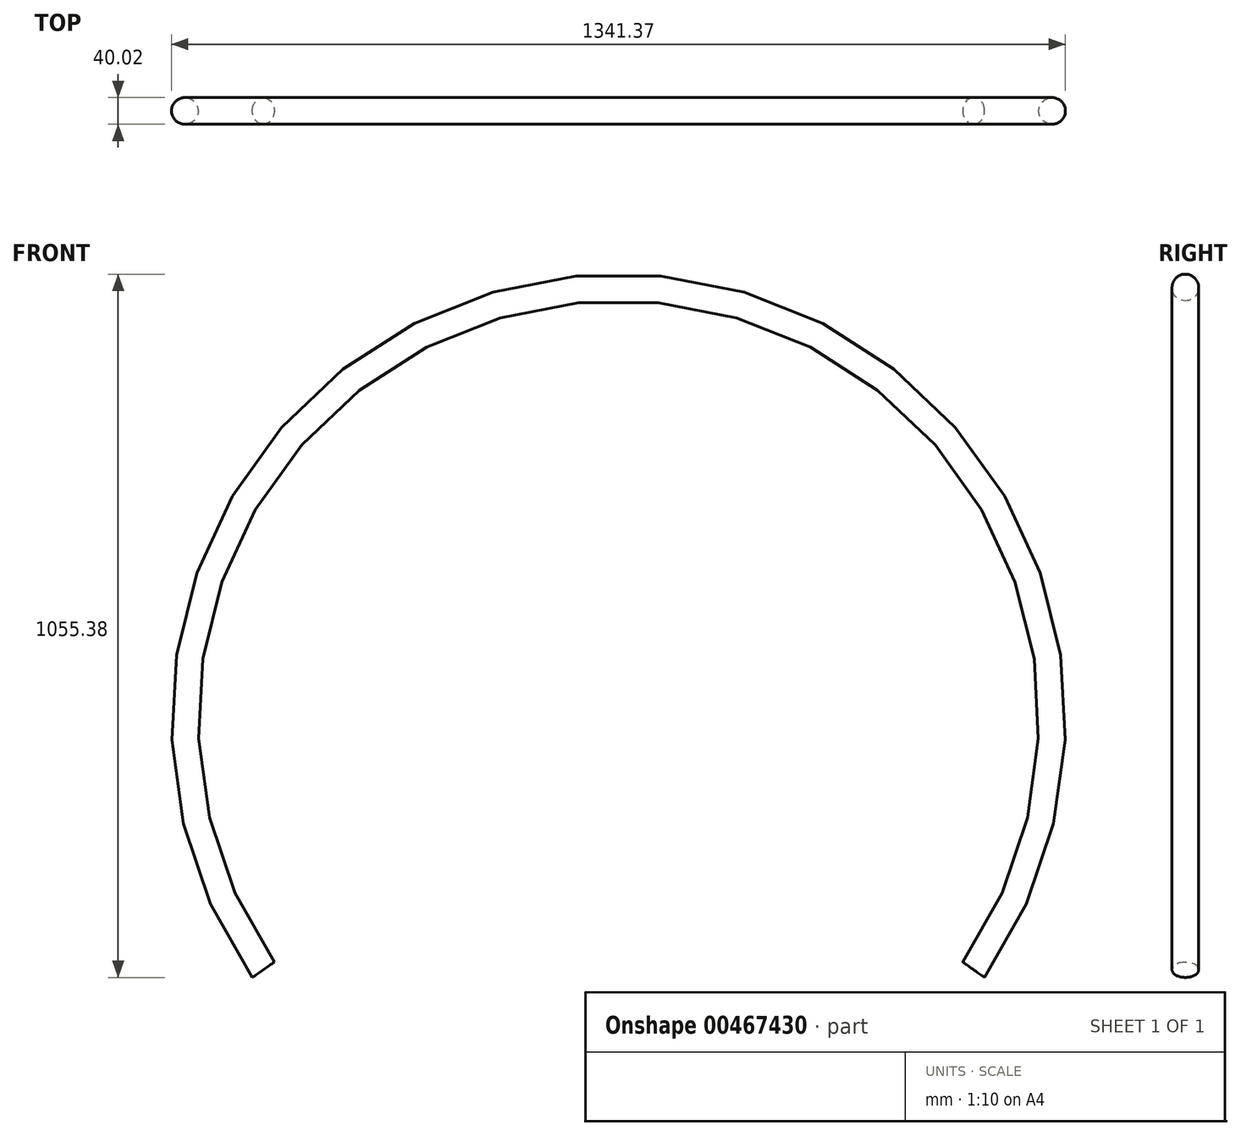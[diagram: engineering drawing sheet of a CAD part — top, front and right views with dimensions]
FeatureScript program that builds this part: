
annotation { "Feature Type Name" : "Feature", "Feature Type Description" : "" }
export const myFeature = defineFeature(function(context is Context, id is Id, definition is map)
    precondition{}
    {
        {
            var Q0;
            Q0=qCreatedBy(makeId("Top.planeOp"),FACE);
            var sketch = newSketch(context, id + "F0", { "sketchPlane" : qUnion([Q0])});
            skLineSegment(sketch, "E0", {"start": v(-745.76, 19.57) * mm, "end": v(-745.76, -19.57) * mm});
            skLineSegment(sketch, "E1", {"start": v(-95.08, 0) * mm, "end": v(-745.76, 0) * mm});
            skCircle(sketch, "E2", {"center": v(-95.08, 0) * mm, "radius": 20 * mm});
            skSolve(sketch);
        }
        {
            var Q0;
            Q0=makeQuery(id+"F0.imprint","IMPRINT",FACE,{"disambiguationData":[TD([[makeQuery(id+"F0.imprint","IMPRINT",EDGE,{"derivedFrom":sQuery(id+"F0.wireOp",EDGE,"c4GEaKpM-oBZo-XXvf-vIMQ-O9dzgLv3TFdV")}),1.0]])]});
            var Q1;
            Q1=makeQuery(id+"F0.imprint","IMPRINT",FACE,{"disambiguationData":[TD([[makeQuery(id+"F0.imprint","IMPRINT",EDGE,{"derivedFrom":sQuery(id+"F0.wireOp",EDGE,"E2")}),1.0]])]});
            var Q2;
            Q2=sQuery(id+"F0.wireOp",EDGE,"E0");
            revolve(context, id + "F1", {"entities" : qUnion([Q0, Q1]), "axis" : qUnion([Q2]), "revolveType" : RevolveType.TWO_DIRECTIONS, "angle" : 215 * degree, "angleBack" : 325 * degree});
        }
    });
